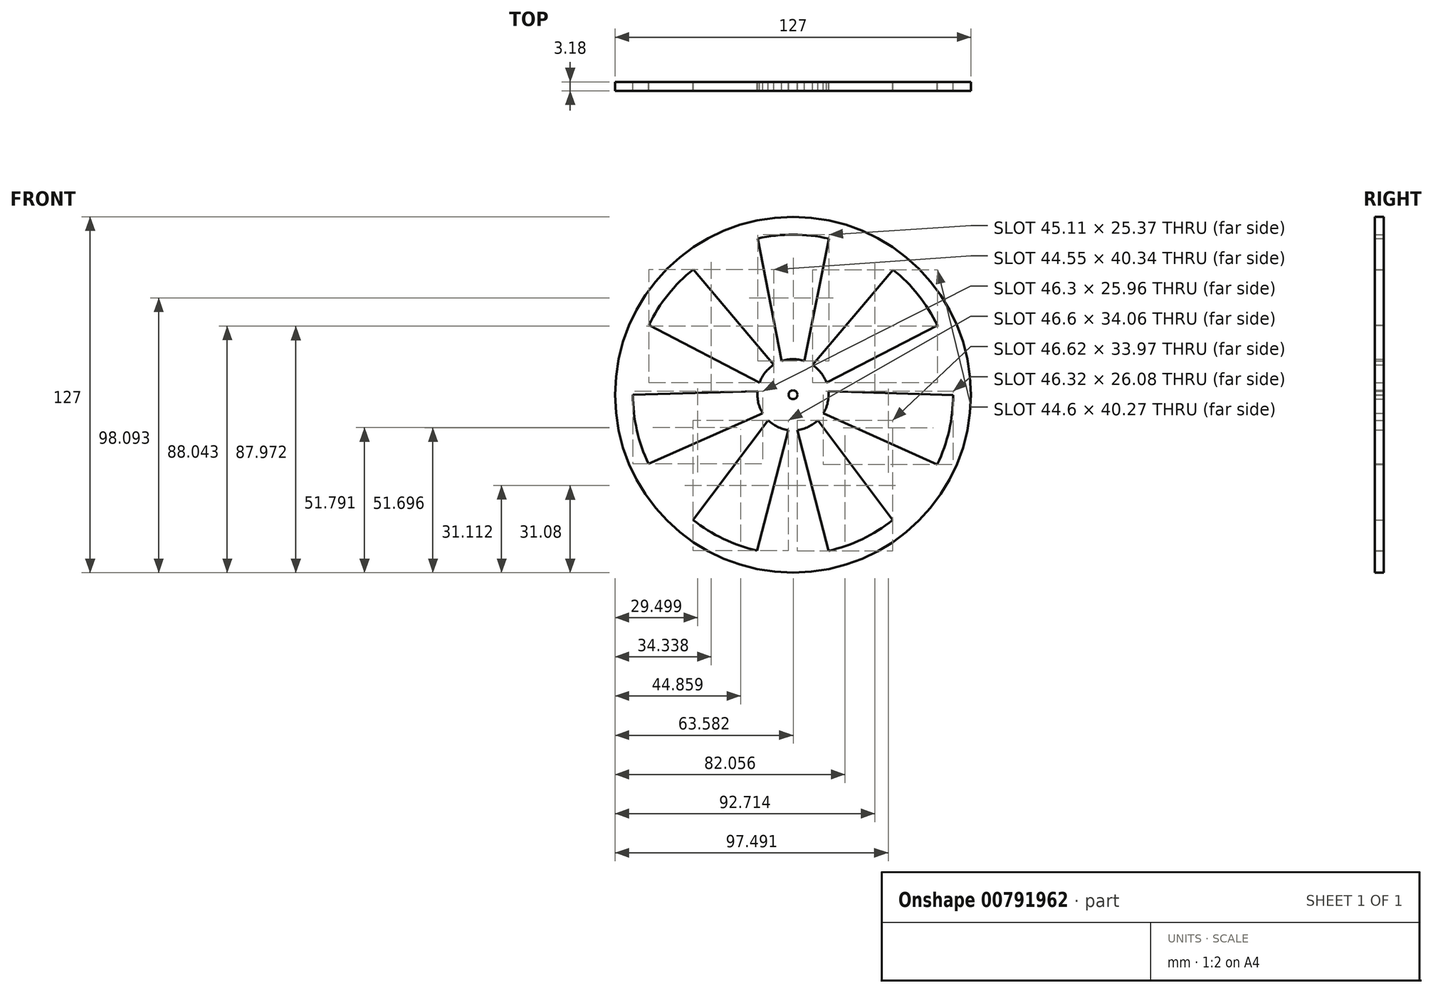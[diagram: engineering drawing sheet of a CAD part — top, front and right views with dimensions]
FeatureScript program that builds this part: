
annotation { "Feature Type Name" : "Feature", "Feature Type Description" : "" }
export const myFeature = defineFeature(function(context is Context, id is Id, definition is map)
    precondition{}
    {
        {
            var Q0;
            Q0=qCreatedBy(makeId("Front.planeOp"),FACE);
            var sketch = newSketch(context, id + "F0", { "sketchPlane" : qUnion([Q0])});
            skArc(sketch, "E0", {"start": v(12.77, 55.7) * mm, "mid": v(0.08, 57.15) * mm, "end": v(-12.6, 55.74) * mm});
            skCircle(sketch, "E1", {"center": v(0, 0) * mm, "radius": 63.5 * mm});
            skArc(sketch, "E2", {"start": v(4.05, 12.04) * mm, "mid": v(0.02, 12.7) * mm, "end": v(-4.02, 12.05) * mm});
            skLineSegment(sketch, "E3", {"start": v(-12.6, 55.74) * mm, "end": v(-4.02, 12.05) * mm});
            skLineSegment(sketch, "E4", {"start": v(12.77, 55.7) * mm, "end": v(4.05, 12.04) * mm});
            skArc(sketch, "E5.1.0", {"start": v(-35.6, 44.71) * mm, "mid": v(-44.63, 35.7) * mm, "end": v(-51.44, 24.9) * mm});
            skLineSegment(sketch, "E5.1.1", {"start": v(-51.44, 24.9) * mm, "end": v(-11.92, 4.37) * mm});
            skLineSegment(sketch, "E5.1.2", {"start": v(-35.6, 44.71) * mm, "end": v(-6.88, 10.67) * mm});
            skArc(sketch, "E5.1.3", {"start": v(-6.88, 10.67) * mm, "mid": v(-9.92, 7.93) * mm, "end": v(-11.92, 4.37) * mm});
            skArc(sketch, "E5.2.0", {"start": v(-57.15, 0.05) * mm, "mid": v(-55.74, -12.63) * mm, "end": v(-51.54, -24.69) * mm});
            skLineSegment(sketch, "E5.2.1", {"start": v(-51.54, -24.69) * mm, "end": v(-10.85, -6.6) * mm});
            skLineSegment(sketch, "E5.2.2", {"start": v(-57.15, 0.05) * mm, "end": v(-12.64, 1.27) * mm});
            skArc(sketch, "E5.2.3", {"start": v(-12.64, 1.27) * mm, "mid": v(-12.39, -2.8) * mm, "end": v(-10.85, -6.6) * mm});
            skArc(sketch, "E5.3.0", {"start": v(-35.67, -44.65) * mm, "mid": v(-24.87, -51.45) * mm, "end": v(-12.83, -55.7) * mm});
            skLineSegment(sketch, "E5.3.1", {"start": v(-12.83, -55.7) * mm, "end": v(-1.6, -12.6) * mm});
            skLineSegment(sketch, "E5.3.2", {"start": v(-35.67, -44.65) * mm, "end": v(-8.87, -9.09) * mm});
            skArc(sketch, "E5.3.3", {"start": v(-8.87, -9.09) * mm, "mid": v(-5.53, -11.43) * mm, "end": v(-1.6, -12.6) * mm});
            skArc(sketch, "E5.4.0", {"start": v(12.67, -55.73) * mm, "mid": v(24.72, -51.53) * mm, "end": v(35.54, -44.76) * mm});
            skLineSegment(sketch, "E5.4.1", {"start": v(35.54, -44.76) * mm, "end": v(8.85, -9.11) * mm});
            skLineSegment(sketch, "E5.4.2", {"start": v(12.67, -55.73) * mm, "end": v(1.57, -12.6) * mm});
            skArc(sketch, "E5.4.3", {"start": v(1.57, -12.6) * mm, "mid": v(5.5, -11.45) * mm, "end": v(8.85, -9.11) * mm});
            skArc(sketch, "E5.5.0", {"start": v(51.47, -24.84) * mm, "mid": v(55.7, -12.8) * mm, "end": v(57.15, -0.12) * mm});
            skLineSegment(sketch, "E5.5.1", {"start": v(57.15, -0.12) * mm, "end": v(12.64, 1.23) * mm});
            skLineSegment(sketch, "E5.5.2", {"start": v(51.47, -24.84) * mm, "end": v(10.83, -6.63) * mm});
            skArc(sketch, "E5.5.3", {"start": v(10.83, -6.63) * mm, "mid": v(12.38, -2.84) * mm, "end": v(12.64, 1.23) * mm});
            skArc(sketch, "E5.6.0", {"start": v(51.51, 24.75) * mm, "mid": v(44.73, 35.57) * mm, "end": v(35.72, 44.6) * mm});
            skLineSegment(sketch, "E5.6.1", {"start": v(35.72, 44.6) * mm, "end": v(6.92, 10.65) * mm});
            skLineSegment(sketch, "E5.6.2", {"start": v(51.51, 24.75) * mm, "end": v(11.94, 4.34) * mm});
            skArc(sketch, "E5.6.3", {"start": v(11.94, 4.34) * mm, "mid": v(9.94, 7.9) * mm, "end": v(6.92, 10.65) * mm});
            skCircle(sketch, "E6", {"center": v(0, 0) * mm, "radius": 1.59 * mm});
            skSolve(sketch);
        }
        {
            var Q0;
            Q0=makeQuery(id+"F0.imprint","IMPRINT",FACE,{"disambiguationData":[TD([[makeQuery(id+"F0.imprint","IMPRINT",EDGE,{"derivedFrom":sQuery(id+"F0.wireOp",EDGE,"E0")}),-1.0]])]});
            extrude(context, id + "F1", {"entities" : qUnion([Q0]), "depth" : 3.17 * mm, "offsetDistance" : 25.4 * mm});
        }
    });
